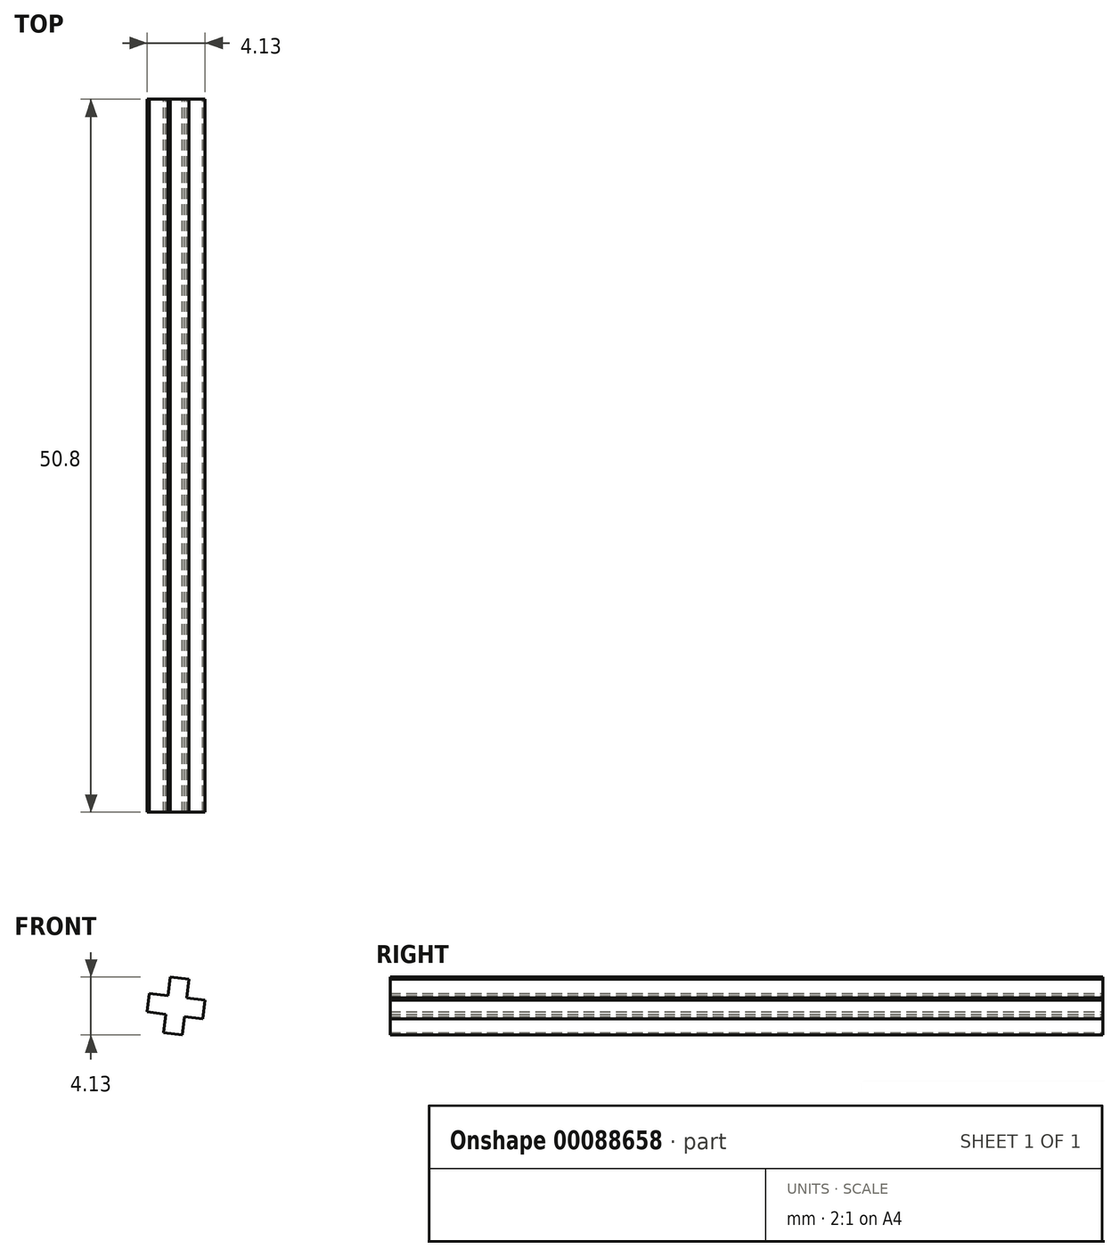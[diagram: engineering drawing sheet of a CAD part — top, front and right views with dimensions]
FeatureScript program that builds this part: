
annotation { "Feature Type Name" : "Feature", "Feature Type Description" : "" }
export const myFeature = defineFeature(function(context is Context, id is Id, definition is map)
    precondition{}
    {
        {
            var Q0;
            Q0=qCreatedBy(makeId("Front.planeOp"),FACE);
            var sketch = newSketch(context, id + "F0", { "sketchPlane" : qUnion([Q0])});
            skLineSegment(sketch, "E0", {"start": v(-31.05, -5.95) * mm, "end": v(-32.02, -13.9) * mm, "construction": true});
            skLineSegment(sketch, "E1", {"start": v(-30.63, -8.02) * mm, "end": v(-30.8, -9.34) * mm});
            skLineSegment(sketch, "E2", {"start": v(-30.8, -9.34) * mm, "end": v(-29.47, -9.5) * mm});
            skLineSegment(sketch, "E3", {"start": v(-29.47, -9.5) * mm, "end": v(-29.55, -10.17) * mm});
            skLineSegment(sketch, "E4", {"start": v(-30.63, -8.02) * mm, "end": v(-31.3, -7.94) * mm});
            skLineSegment(sketch, "E5", {"start": v(-27.56, -10.41) * mm, "end": v(-33.4, -9.7) * mm, "construction": true});
            skLineSegment(sketch, "E6.MirrorCS", {"start": v(-31.12, -12) * mm, "end": v(-31.78, -11.9) * mm});
            skLineSegment(sketch, "E7.MirrorCS", {"start": v(-31.12, -12) * mm, "end": v(-30.95, -10.67) * mm});
            skLineSegment(sketch, "E8.MirrorCS", {"start": v(-30.95, -10.67) * mm, "end": v(-29.63, -10.83) * mm});
            skLineSegment(sketch, "E9.MirrorCS", {"start": v(-29.63, -10.83) * mm, "end": v(-29.55, -10.17) * mm});
            skLineSegment(sketch, "E10.MirrorCS", {"start": v(-31.95, -7.86) * mm, "end": v(-31.3, -7.94) * mm});
            skLineSegment(sketch, "E11.MirrorCS", {"start": v(-31.95, -7.86) * mm, "end": v(-32.11, -9.18) * mm});
            skLineSegment(sketch, "E12.MirrorCS", {"start": v(-32.11, -9.18) * mm, "end": v(-33.44, -9.02) * mm});
            skLineSegment(sketch, "E13.MirrorCS", {"start": v(-33.44, -9.02) * mm, "end": v(-33.52, -9.68) * mm});
            skLineSegment(sketch, "E14.MirrorCS", {"start": v(-33.6, -10.34) * mm, "end": v(-33.52, -9.68) * mm});
            skLineSegment(sketch, "E15.MirrorCS", {"start": v(-32.28, -10.5) * mm, "end": v(-33.6, -10.34) * mm});
            skLineSegment(sketch, "E16.MirrorCS", {"start": v(-32.44, -11.83) * mm, "end": v(-32.28, -10.5) * mm});
            skLineSegment(sketch, "E17.MirrorCS", {"start": v(-32.44, -11.83) * mm, "end": v(-31.78, -11.9) * mm});
            skSolve(sketch);
        }
        {
            var Q0;
            Q0 = qSketchRegion(id + "F0", true);
            extrude(context, id + "F1", {"entities" : qUnion([Q0]), "depth" : 50.8 * mm});
        }
    });
